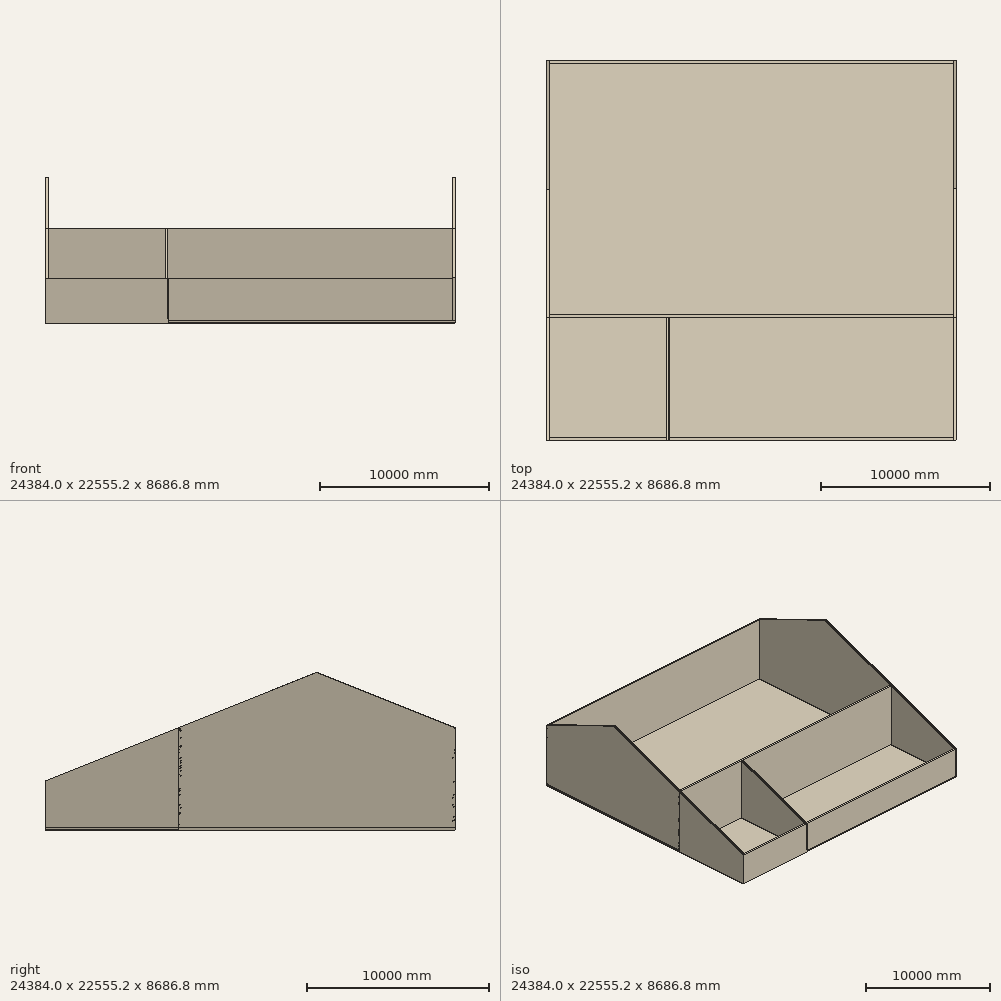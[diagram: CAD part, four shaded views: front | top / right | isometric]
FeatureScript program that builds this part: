
annotation { "Feature Type Name" : "Feature", "Feature Type Description" : "" }
export const myFeature = defineFeature(function(context is Context, id is Id, definition is map)
    precondition{}
    {
        {
            var Q0;
            Q0=qCreatedBy(makeId("Top.planeOp"),FACE);
            var sketch = newSketch(context, id + "F0", { "sketchPlane" : qUnion([Q0])});
            skLineSegment(sketch, "E0.rect.bottom", {"start": v(-12192, -7620) * mm, "end": v(12192, -7620) * mm});
            skLineSegment(sketch, "E0.rect.top", {"start": v(-12192, 7620) * mm, "end": v(12192, 7620) * mm});
            skLineSegment(sketch, "E0.rect.left", {"start": v(-12192, -7620) * mm, "end": v(-12192, 7620) * mm});
            skLineSegment(sketch, "E0.rect.right", {"start": v(12192, -7620) * mm, "end": v(12192, 7620) * mm});
            skPoint(sketch, "E0.rect.middle", {"position": v(0, 0) * mm});
            skSolve(sketch);
        }
        {
            var Q0;
            Q0=qSketchRegion(id+"F0",true);
            extrude(context, id + "F1", {"entities" : qUnion([Q0]), "depth" : 152.4 * mm});
        }
        {
            var Q0;
            Q0=makeQuery(id+"F1.opExtrude","SWEPT_FACE",FACE,{"disambiguationData":[OSD([sQuery(id+"F0.wireOp",EDGE,"E0.rect.bottom")])]});
            var sketch = newSketch(context, id + "F2", { "sketchPlane" : qUnion([Q0])});
            skLineSegment(sketch, "E1", {"start": v(-12192, 152.4) * mm, "end": v(-12192, 5638.8) * mm});
            skLineSegment(sketch, "E2", {"start": v(-12192, 5638.8) * mm, "end": v(12192, 5638.8) * mm});
            skLineSegment(sketch, "E3", {"start": v(12192, 152.4) * mm, "end": v(12192, 5638.8) * mm});
            skSolve(sketch);
        }
        {
            var Q0;
            Q0=makeQuery(id+"F2.imprint","IMPRINT",FACE,{"disambiguationData":[TD([[makeQuery(id+"F2.imprint","IMPRINT",EDGE,{"derivedFrom":sQuery(id+"F2.wireOp",EDGE,"E1")}),-1.0]])]});
            extrude(context, id + "F3", {"entities" : qUnion([Q0]), "oppositeDirection" : true, "depth" : 152.4 * mm});
        }
        {
            var Q0;
            Q0=makeQuery(id+"F1.opExtrude","SWEPT_FACE",FACE,{"disambiguationData":[OSD([sQuery(id+"F0.wireOp",EDGE,"E0.rect.top")])]});
            var sketch = newSketch(context, id + "F4", { "sketchPlane" : qUnion([Q0])});
            skLineSegment(sketch, "E4", {"start": v(-12192, 152.4) * mm, "end": v(-12192, 5638.8) * mm});
            skLineSegment(sketch, "E5", {"start": v(-12192, 152.4) * mm, "end": v(12192, 152.4) * mm});
            skLineSegment(sketch, "E6", {"start": v(12192, 152.4) * mm, "end": v(12192, 5638.8) * mm});
            skLineSegment(sketch, "E7", {"start": v(12192, 5638.8) * mm, "end": v(-12192, 5638.8) * mm});
            skSolve(sketch);
        }
        {
            var Q0;
            Q0=qSketchRegion(id+"F4",true);
            extrude(context, id + "F5", {"entities" : qUnion([Q0]), "oppositeDirection" : true, "depth" : 152.4 * mm});
        }
        {
            var Q0;
            Q0=makeQuery(id+"F1.opExtrude","SWEPT_FACE",FACE,{"disambiguationData":[OSD([sQuery(id+"F0.wireOp",EDGE,"E0.rect.right")])]});
            var sketch = newSketch(context, id + "F6", { "sketchPlane" : qUnion([Q0])});
            skLineSegment(sketch, "E8", {"start": v(-7620, 152.4) * mm, "end": v(-7620, 5638.8) * mm});
            skLineSegment(sketch, "E9", {"start": v(-7620, 5638.8) * mm, "end": v(7620, 5638.8) * mm});
            skLineSegment(sketch, "E10", {"start": v(7620, 5638.8) * mm, "end": v(7620, 152.4) * mm});
            skLineSegment(sketch, "E11", {"start": v(7620, 152.4) * mm, "end": v(-7620, 152.4) * mm});
            skLineSegment(sketch, "E12", {"start": v(0, 152.4) * mm, "end": v(0, 8686.8) * mm, "construction": true});
            skPoint(sketch, "E12.endSnap0", {"position": v(0, 152.4) * mm});
            skLineSegment(sketch, "E13", {"start": v(-7620, 5638.8) * mm, "end": v(0, 8686.8) * mm});
            skLineSegment(sketch, "E14", {"start": v(0, 8686.8) * mm, "end": v(7620, 5638.8) * mm});
            skPoint(sketch, "E15", {"position": v(0, 5638.8) * mm});
            skSolve(sketch);
        }
        {
            var Q0;
            Q0=qSketchRegion(id+"F6",true);
            extrude(context, id + "F7", {"entities" : qUnion([Q0]), "oppositeDirection" : true, "depth" : 152.4 * mm});
        }
        {
            var Q0;
            Q0=makeQuery(id+"F1.opExtrude","SWEPT_FACE",FACE,{"disambiguationData":[OSD([sQuery(id+"F0.wireOp",EDGE,"E0.rect.left")])]});
            var sketch = newSketch(context, id + "F8", { "sketchPlane" : qUnion([Q0])});
            skLineSegment(sketch, "E16", {"start": v(-7620, 152.4) * mm, "end": v(-7620, 5638.8) * mm});
            skLineSegment(sketch, "E17", {"start": v(-7620, 5638.8) * mm, "end": v(7620, 5638.8) * mm});
            skLineSegment(sketch, "E18", {"start": v(7620, 5638.8) * mm, "end": v(7620, 152.4) * mm});
            skLineSegment(sketch, "E19", {"start": v(7620, 152.4) * mm, "end": v(-7620, 152.4) * mm});
            skLineSegment(sketch, "E20", {"start": v(27.36, -1119.3) * mm, "end": v(27.36, 8686.8) * mm, "construction": true});
            skPoint(sketch, "E20.endSnap0", {"position": v(27.36, 169.92) * mm});
            skLineSegment(sketch, "E21", {"start": v(-7620, 5638.8) * mm, "end": v(27.36, 8686.8) * mm});
            skLineSegment(sketch, "E22", {"start": v(27.36, 8686.8) * mm, "end": v(7620, 5638.8) * mm});
            skPoint(sketch, "E23", {"position": v(0, 5638.8) * mm});
            skSolve(sketch);
        }
        {
            var Q0;
            Q0=qSketchRegion(id+"F8",true);
            extrude(context, id + "F9", {"entities" : qUnion([Q0]), "oppositeDirection" : true, "depth" : 152.4 * mm});
        }
        {
            var Q0;
            Q0=makeQuery(id+"F1.opExtrude","CAP_FACE",FACE,{"disambiguationData":[OSD([sQuery(id+"F0.wireOp",EDGE,"E0.rect.bottom"),sQuery(id+"F0.wireOp",EDGE,"E0.rect.top"),sQuery(id+"F0.wireOp",EDGE,"E0.rect.left"),sQuery(id+"F0.wireOp",EDGE,"E0.rect.right")])],"isStart":false});
            var sketch = newSketch(context, id + "F10", { "sketchPlane" : qUnion([Q0])});
            skLineSegment(sketch, "E24", {"start": v(-12192, -7620) * mm, "end": v(12192, -7620) * mm});
            skLineSegment(sketch, "E25", {"start": v(-12192, -14935.2) * mm, "end": v(-12192, -7620) * mm});
            skLineSegment(sketch, "E26", {"start": v(-4876.8, -7620) * mm, "end": v(-4876.8, -14935.2) * mm});
            skLineSegment(sketch, "E27", {"start": v(-4876.8, -14935.2) * mm, "end": v(-12192, -14935.2) * mm});
            skSolve(sketch);
        }
        {
            var Q0;
            {var subQ0=sQuery(id+"F10.wireOp",EDGE,"E25");Q0=makeQuery(id+"F10.imprint","IMPRINT",FACE,{"disambiguationData":[TD([[makeQuery(id+"F10.imprint","IMPRINT",EDGE,{"derivedFrom":subQ0}),-1.0]])]});}
            extrude(context, id + "F11", {"entities" : qUnion([Q0]), "endBound" : BoundingType.SYMMETRIC, "depth" : 304.8 * mm});
        }
        {
            var Q0;
            Q0=makeQuery(id+"F1.opExtrude","CAP_FACE",FACE,{"disambiguationData":[OSD([sQuery(id+"F0.wireOp",EDGE,"E0.rect.bottom"),sQuery(id+"F0.wireOp",EDGE,"E0.rect.top"),sQuery(id+"F0.wireOp",EDGE,"E0.rect.left"),sQuery(id+"F0.wireOp",EDGE,"E0.rect.right")])],"isStart":false});
            var sketch = newSketch(context, id + "F12", { "sketchPlane" : qUnion([Q0])});
            skLineSegment(sketch, "E28", {"start": v(12192, -7620) * mm, "end": v(12192, -14935.2) * mm});
            skLineSegment(sketch, "E29", {"start": v(12192, -7620) * mm, "end": v(-4876.8, -7620) * mm});
            skLineSegment(sketch, "E30", {"start": v(-4876.8, -7620) * mm, "end": v(-4876.8, -14935.2) * mm});
            skLineSegment(sketch, "E31", {"start": v(12192, -14935.2) * mm, "end": v(-4876.8, -14935.2) * mm});
            skSolve(sketch);
        }
        {
            var Q0;
            Q0 = qSketchRegion(id + "F12", true);
            extrude(context, id + "F13", {"entities" : qUnion([Q0]), "oppositeDirection" : true, "depth" : 101.6 * mm});
        }
        {
            var Q0;
            Q0=makeQuery(id+"F11.opExtrude","SWEPT_FACE",FACE,{"disambiguationData":[OSD([sQuery(id+"F10.wireOp",EDGE,"E25")])]});
            var sketch = newSketch(context, id + "F14", { "sketchPlane" : qUnion([Q0])});
            skLineSegment(sketch, "E32", {"start": v(7620, 304.8) * mm, "end": v(14935.2, 304.8) * mm});
            skLineSegment(sketch, "E33", {"start": v(7620, 304.8) * mm, "end": v(7620, 5638.8) * mm});
            skLineSegment(sketch, "E34", {"start": v(7620, 5638.8) * mm, "end": v(14935.2, 2702.18) * mm});
            skLineSegment(sketch, "E35", {"start": v(14935.2, 304.8) * mm, "end": v(14935.2, 2702.18) * mm});
            skLineSegment(sketch, "E36", {"start": v(14935.2, 2702.18) * mm, "end": v(7620, 2702.18) * mm});
            skSolve(sketch);
        }
        {
            var Q0;
            {var subQ0=sQuery(id+"F14.wireOp",EDGE,"E34");Q0=makeQuery(id+"F14.imprint","IMPRINT",FACE,{"disambiguationData":[TD([[makeQuery(id+"F14.imprint","IMPRINT",EDGE,{"derivedFrom":subQ0}),-1.0]])]});}
            var Q1;
            {var subQ0=sQuery(id+"F14.wireOp",EDGE,"E32");Q1=makeQuery(id+"F14.imprint","IMPRINT",FACE,{"disambiguationData":[TD([[makeQuery(id+"F14.imprint","IMPRINT",EDGE,{"derivedFrom":subQ0}),-1.0]])]});}
            extrude(context, id + "F15", {"entities" : qUnion([Q0, Q1]), "oppositeDirection" : true, "depth" : 152.4 * mm});
        }
        {
            var Q0;
            Q0=makeQuery(id+"F15.opExtrude","SWEPT_BODY",BODY,{"disambiguationData":[OSD([sQuery(id+"F14.wireOp",EDGE,"E32"),sQuery(id+"F14.wireOp",EDGE,"E33"),sQuery(id+"F14.wireOp",EDGE,"E34"),sQuery(id+"F14.wireOp",EDGE,"E35")])]});
            transform(context, id + "F16", {"entities" : qUnion([Q0]), "transformType" : TransformType.TRANSLATION_3D, "dx" : 7112 * mm, "dy" : 0 * mm, "dz" : 0 * mm, "makeCopy" : true});
        }
        {
            var Q0;
            Q0=makeQuery(id+"F13.opExtrude","SWEPT_FACE",FACE,{"disambiguationData":[OSD([sQuery(id+"F12.wireOp",EDGE,"E28")])]});
            var sketch = newSketch(context, id + "F17", { "sketchPlane" : qUnion([Q0])});
            skLineSegment(sketch, "E37", {"start": v(-7620, 152.4) * mm, "end": v(-7620, 5638.8) * mm});
            skLineSegment(sketch, "E38", {"start": v(-7620, 152.4) * mm, "end": v(-14935.2, 152.4) * mm});
            skLineSegment(sketch, "E39", {"start": v(-14935.2, 152.4) * mm, "end": v(-14935.2, 2712.72) * mm});
            skLineSegment(sketch, "E40", {"start": v(-14935.2, 2712.72) * mm, "end": v(-7620, 5638.8) * mm});
            skSolve(sketch);
        }
        {
            var Q0;
            Q0 = qSketchRegion(id + "F17", true);
            extrude(context, id + "F18", {"entities" : qUnion([Q0]), "oppositeDirection" : true, "depth" : 152.4 * mm});
        }
        {
            var Q0;
            Q0=makeQuery(id+"F11.opExtrude","SWEPT_FACE",FACE,{"disambiguationData":[OSD([sQuery(id+"F10.wireOp",EDGE,"E27")])]});
            var sketch = newSketch(context, id + "F19", { "sketchPlane" : qUnion([Q0])});
            skLineSegment(sketch, "E41", {"start": v(-12039.6, 304.8) * mm, "end": v(-4876.8, 304.8) * mm});
            skLineSegment(sketch, "E42", {"start": v(-4876.8, 304.8) * mm, "end": v(-4876.8, 2700.93) * mm});
            skLineSegment(sketch, "E43", {"start": v(-4876.8, 2700.93) * mm, "end": v(-12192, 2700.93) * mm});
            skLineSegment(sketch, "E44", {"start": v(-12192, 2700.93) * mm, "end": v(-12192, 304.8) * mm});
            skLineSegment(sketch, "E45", {"start": v(-12039.6, 304.8) * mm, "end": v(-12039.6, 2700.93) * mm});
            skPoint(sketch, "E46", {"position": v(-5029.2, 304.8) * mm});
            skLineSegment(sketch, "E47", {"start": v(-5029.2, 304.8) * mm, "end": v(-5029.2, 2700.93) * mm});
            skSolve(sketch);
        }
        {
            var Q0;
            {var subQ0=sQuery(id+"F19.wireOp",EDGE,"E45");Q0=makeQuery(id+"F19.imprint","IMPRINT",FACE,{"disambiguationData":[TD([[makeQuery(id+"F19.imprint","IMPRINT",EDGE,{"derivedFrom":subQ0}),-1.0]])]});}
            extrude(context, id + "F20", {"entities" : qUnion([Q0]), "operationType" : NewBodyOperationType.ADD, "oppositeDirection" : true, "depth" : 152.4 * mm});
        }
        {
            var Q0;
            Q0=makeQuery(id+"F13.opExtrude","SWEPT_FACE",FACE,{"disambiguationData":[OSD([sQuery(id+"F12.wireOp",EDGE,"E31")])]});
            var sketch = newSketch(context, id + "F21", { "sketchPlane" : qUnion([Q0])});
            skLineSegment(sketch, "E48", {"start": v(-4876.8, 152.4) * mm, "end": v(12192, 152.4) * mm});
            skLineSegment(sketch, "E49", {"start": v(12192, 152.4) * mm, "end": v(12192, 2700.93) * mm});
            skLineSegment(sketch, "E50", {"start": v(12192, 2700.93) * mm, "end": v(-4876.8, 2700.93) * mm});
            skLineSegment(sketch, "E51", {"start": v(-4876.8, 2700.93) * mm, "end": v(-4876.8, 152.4) * mm});
            skLineSegment(sketch, "E52", {"start": v(12039.6, 152.4) * mm, "end": v(12039.6, 2700.93) * mm});
            skSolve(sketch);
        }
        {
            var Q0;
            {var subQ0=sQuery(id+"F21.wireOp",EDGE,"E51");Q0=makeQuery(id+"F21.imprint","IMPRINT",FACE,{"disambiguationData":[TD([[makeQuery(id+"F21.imprint","IMPRINT",EDGE,{"derivedFrom":subQ0}),1.0]])]});}
            extrude(context, id + "F22", {"entities" : qUnion([Q0]), "oppositeDirection" : true, "depth" : 152.4 * mm});
        }
    });
